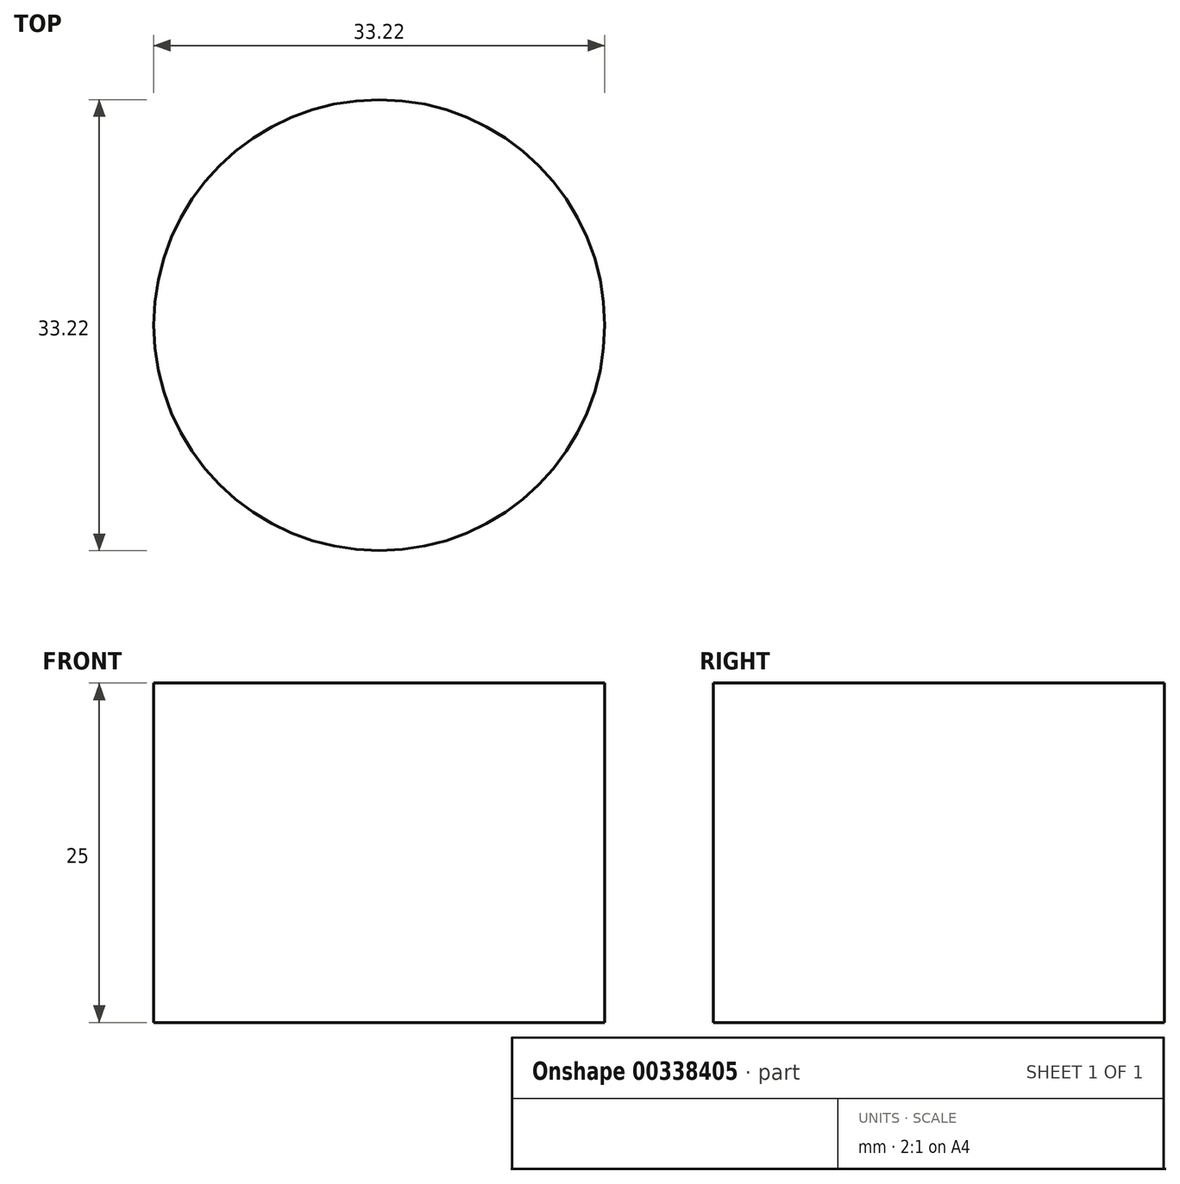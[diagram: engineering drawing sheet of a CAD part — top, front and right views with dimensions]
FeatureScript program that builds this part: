
annotation { "Feature Type Name" : "Feature", "Feature Type Description" : "" }
export const myFeature = defineFeature(function(context is Context, id is Id, definition is map)
    precondition{}
    {
        {
            var Q0;
            Q0=qCreatedBy(makeId("Top.planeOp"),FACE);
            var sketch = newSketch(context, id + "F0", { "sketchPlane" : qUnion([Q0])});
            skCircle(sketch, "E0", {"center": v(0, 0) * mm, "radius": 16.6 * mm});
            skSolve(sketch);
        }
        {
            var Q0;
            Q0=makeQuery(id+"F0.imprint","IMPRINT",FACE,{"disambiguationData":[TD([[makeQuery(id+"F0.imprint","IMPRINT",EDGE,{"derivedFrom":sQuery(id+"F0.wireOp",EDGE,"E0")}),1.0]])]});
            extrude(context, id + "F1", {"entities" : qUnion([Q0]), "depth" : 25 * mm});
        }
    });
